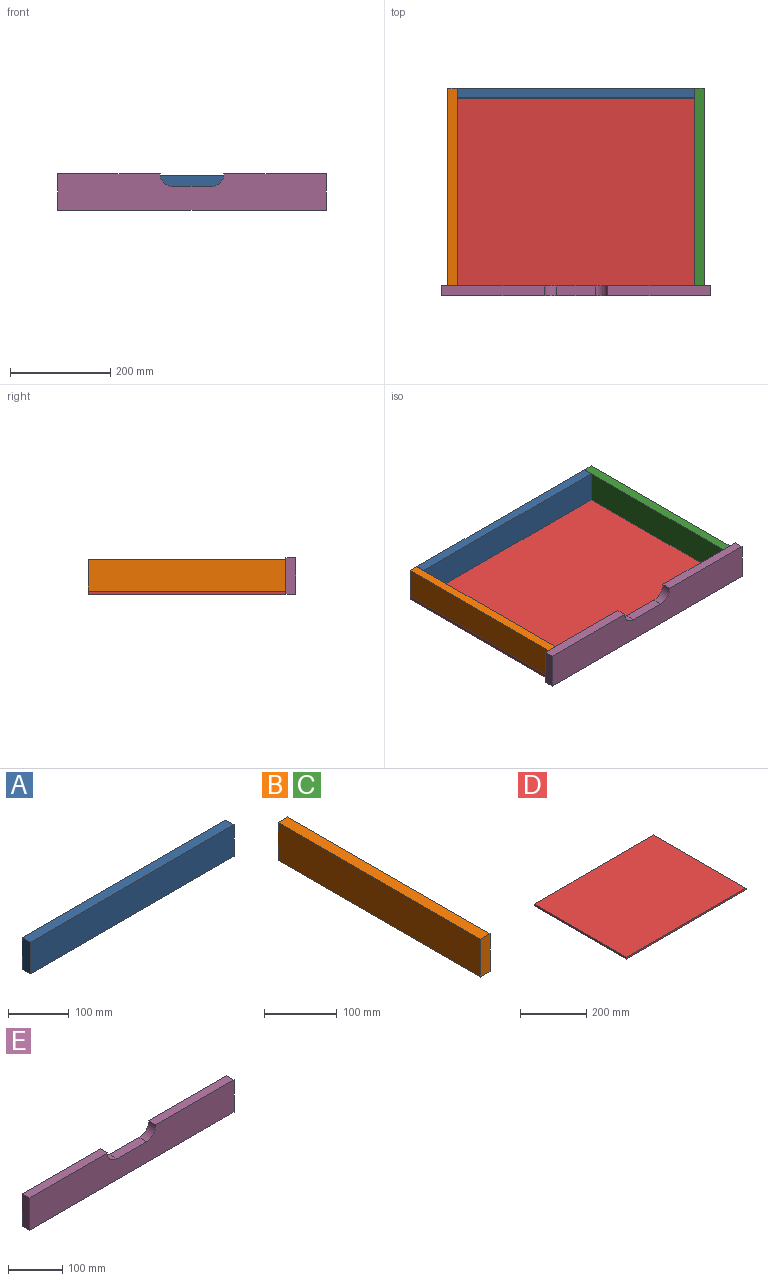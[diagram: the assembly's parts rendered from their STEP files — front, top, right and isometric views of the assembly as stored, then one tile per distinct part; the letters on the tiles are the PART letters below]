
ASSEMBLY  parts=5 mates=4
PART A: 6 faces, bbox 473.1x19.1x63.5 mm
  f0: plane 63.5x19.05mm, normal (1,0,0), area 1209.7mm2, adj f1,f3,f4,f5
  f1: plane 473.08x19.05mm, normal (0,0,1), area 9012.1mm2, adj f0,f2,f4,f5
  f2: plane 63.5x19.05mm, normal (-1,0,0), area 1209.7mm2, adj f1,f3,f4,f5
  f3: plane 473.08x19.05mm, normal (0,0,-1), area 9012.1mm2, adj f0,f2,f4,f5
  f4: plane 473.08x63.5mm, normal (0,-1,0), area 30040.3mm2, adj f0,f1,f2,f3
  f5: plane 473.08x63.5mm, normal (0,1,0), area 30040.3mm2, adj f0,f1,f2,f3
PART B: 6 faces, bbox 19.1x393.7x63.5 mm
  f0: plane 63.5x19.05mm, normal (0,1,0), area 1209.7mm2, adj f1,f3,f4,f5
  f1: plane 393.7x19.05mm, normal (0,0,1), area 7500mm2, adj f0,f2,f4,f5
  f2: plane 63.5x19.05mm, normal (0,-1,0), area 1209.7mm2, adj f1,f3,f4,f5
  f3: plane 393.7x19.05mm, normal (0,0,-1), area 7500mm2, adj f0,f2,f4,f5
  f4: plane 393.7x63.5mm, normal (1,0,0), area 24999.9mm2, adj f0,f1,f2,f3
  f5: plane 393.7x63.5mm, normal (-1,0,0), area 24999.9mm2, adj f0,f1,f2,f3
PART C: same geometry as B
PART D: 6 faces, bbox 511.2x393.7x6.4 mm
  f0: plane 393.7x6.35mm, normal (1,0,0), area 2500mm2, adj f1,f3,f4,f5
  f1: plane 511.18x6.35mm, normal (0,1,0), area 3246mm2, adj f0,f2,f4,f5
  f2: plane 393.7x6.35mm, normal (-1,0,0), area 2500mm2, adj f1,f3,f4,f5
  f3: plane 511.18x6.35mm, normal (0,-1,0), area 3246mm2, adj f0,f2,f4,f5
  f4: plane 511.18x393.7mm, normal (0,0,1), area 201249.6mm2, adj f0,f1,f2,f3
  f5: plane 511.18x393.7mm, normal (0,0,-1), area 201249.6mm2, adj f0,f1,f2,f3
PART E: 10 faces, bbox 535x19.1x73 mm
  f0: plane 73.03x19.05mm, normal (1,0,0), area 1391.1mm2, adj f1,f7,f8,f9
  f1: plane 203.99x19.05mm, normal (0,0,1), area 3886.1mm2, adj f0,f2,f8,f9
  f2: cylinder r=25.4mm len=25.4mm, axis (0,1,0), area 760.1mm2, adj f1,f3,f8,f9
  f3: plane 76.2x19.05mm, normal (0,0,1), area 1451.6mm2, adj f2,f4,f8,f9
  f4: cylinder r=25.4mm len=25.4mm, axis (0,1,0), area 760.1mm2, adj f3,f5,f8,f9
  f5: plane 203.99x19.05mm, normal (0,0,1), area 3886.1mm2, adj f4,f6,f8,f9
  f6: plane 73.03x19.05mm, normal (-1,0,0), area 1391.1mm2, adj f5,f7,f8,f9
  f7: plane 534.99x19.05mm, normal (0,0,-1), area 10191.5mm2, adj f0,f6,f8,f9
  f8: plane 534.99x73.03mm, normal (0,-1,0), area 36118.6mm2, adj f0,f1,f2,f3,f4,f5,f6,f7
  f9: plane 534.99x73.03mm, normal (0,1,0), area 36118.6mm2, adj f0,f1,f2,f3,f4,f5,f6,f7
PLACE A t=(-49,194.51,73.85)mm
PLACE B t=(-304.59,-2.34,73.85)mm
PLACE C t=(187.54,-2.34,73.85)mm
PLACE D t=(-49,-2.34,35.75)mm
PLACE E t=(-49,-199.19,72.26)mm
MATE fastened B.f5 <-> D.f2  axis (-1,0,0) through (-304.59,-2.34,42.1)mm
MATE fastened C.f4 <-> D.f0  axis (1,0,0) through (206.59,-2.34,42.1)mm
MATE fastened E.f9 <-> D.f3  axis (0,1,0) through (-49,-199.19,35.75)mm
MATE fastened A.f5 <-> D.f1  axis (0,1,0) through (-49,194.51,42.1)mm
